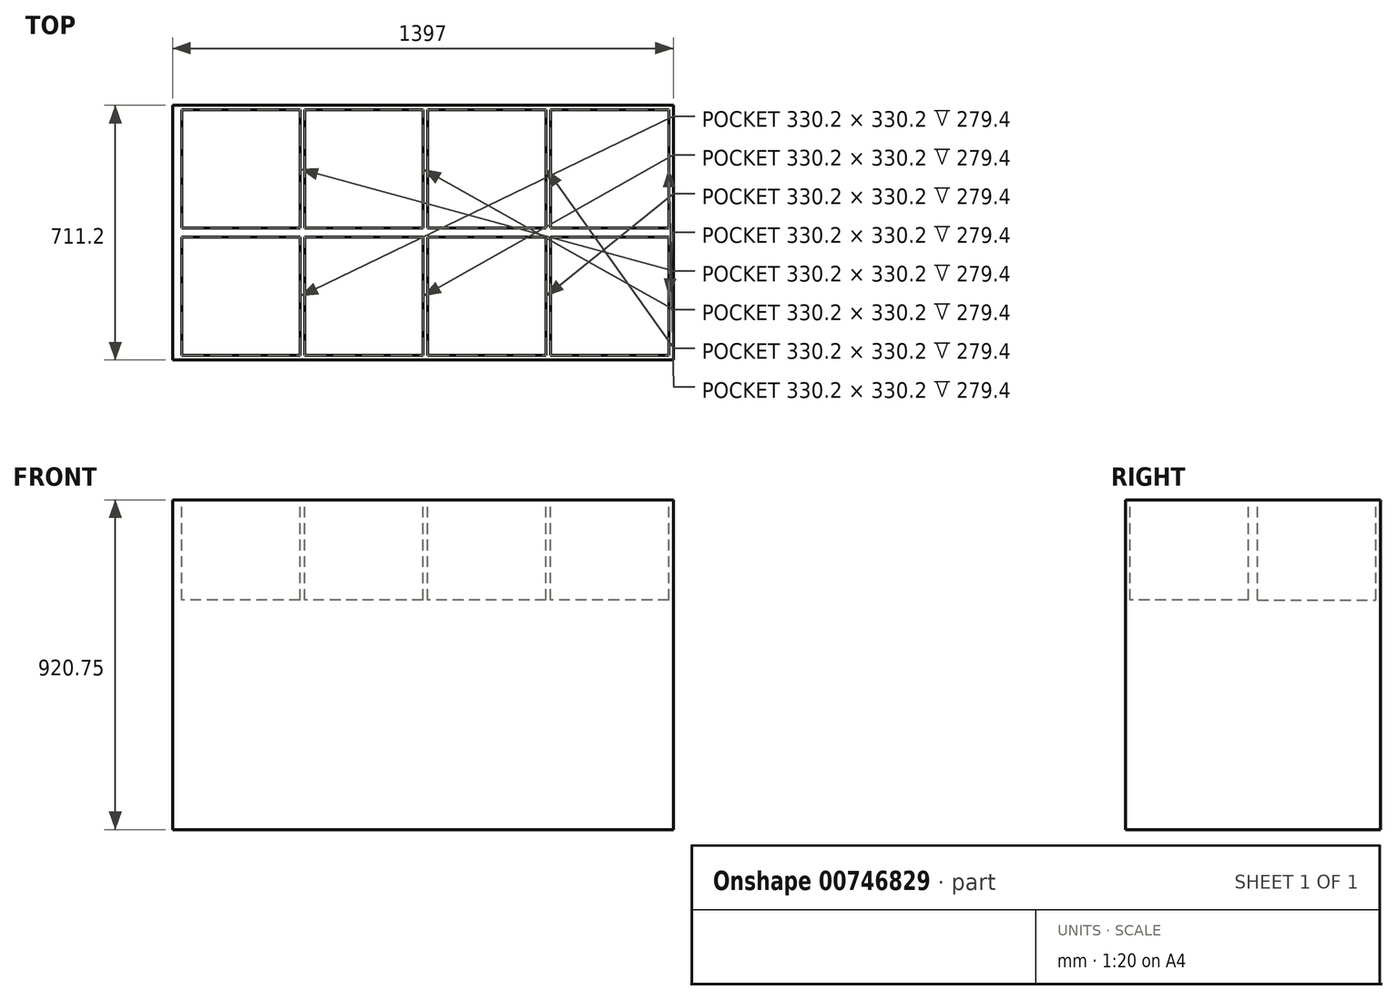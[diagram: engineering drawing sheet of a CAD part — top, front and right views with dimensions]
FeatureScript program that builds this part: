
annotation { "Feature Type Name" : "Feature", "Feature Type Description" : "" }
export const myFeature = defineFeature(function(context is Context, id is Id, definition is map)
    precondition{}
    {
        {
            var Q0;
            Q0=qCreatedBy(makeId("Top.planeOp"),FACE);
            var sketch = newSketch(context, id + "F0", { "sketchPlane" : qUnion([Q0])});
            skLineSegment(sketch, "E0.bottom", {"start": v(0, 0) * mm, "end": v(1397, 0) * mm});
            skLineSegment(sketch, "E0.top", {"start": v(0, -355.6) * mm, "end": v(1397, -355.6) * mm});
            skLineSegment(sketch, "E0.left", {"start": v(0, 0) * mm, "end": v(0, -355.6) * mm});
            skLineSegment(sketch, "E0.right", {"start": v(1397, 0) * mm, "end": v(1397, -355.6) * mm});
            skSolve(sketch);
        }
        {
            var Q0;
            Q0 = qSketchRegion(id + "F0", true);
            extrude(context, id + "F1", {"entities" : qUnion([Q0]), "depth" : 920.75 * mm, "offsetDistance" : 25.4 * mm});
        }
        {
            var Q0;
            Q0=makeQuery(id+"F1.opExtrude","CAP_FACE",FACE,{"disambiguationData":[OSD([sQuery(id+"F0.wireOp",EDGE,"E0.bottom"),sQuery(id+"F0.wireOp",EDGE,"E0.top"),sQuery(id+"F0.wireOp",EDGE,"E0.left"),sQuery(id+"F0.wireOp",EDGE,"E0.right")])],"isStart":false});
            var sketch = newSketch(context, id + "F2", { "sketchPlane" : qUnion([Q0])});
            skLineSegment(sketch, "E1.bottom", {"start": v(1397, -355.6) * mm, "end": v(1384.3, -355.6) * mm});
            skLineSegment(sketch, "E1.top", {"start": v(1397, -342.9) * mm, "end": v(1384.3, -342.9) * mm});
            skLineSegment(sketch, "E1.left", {"start": v(1397, -355.6) * mm, "end": v(1397, -342.9) * mm});
            skLineSegment(sketch, "E1.right", {"start": v(1384.3, -355.6) * mm, "end": v(1384.3, -342.9) * mm});
            skSolve(sketch);
        }
        {
            var Q0;
            {var subQ4=sQuery(id+"F2.wireOp",EDGE,"E1.top");Q0=makeQuery(id+"F2.imprint","IMPRINT",FACE,{"disambiguationData":[TD([[makeQuery(id+"F2.imprint","IMPRINT",EDGE,{"derivedFrom":subQ4}),-1.0]])]});}
            var sketch = newSketch(context, id + "F3", { "sketchPlane" : qUnion([Q0])});
            skLineSegment(sketch, "E2.bottom", {"start": v(1384.3, -342.9) * mm, "end": v(1054.1, -342.9) * mm});
            skLineSegment(sketch, "E2.top", {"start": v(1384.3, -12.7) * mm, "end": v(1054.1, -12.7) * mm});
            skLineSegment(sketch, "E2.left", {"start": v(1384.3, -342.9) * mm, "end": v(1384.3, -12.7) * mm});
            skLineSegment(sketch, "E2.right", {"start": v(1054.1, -342.9) * mm, "end": v(1054.1, -12.7) * mm});
            skSolve(sketch);
        }
        {
            var Q0;
            {var subQ4=sQuery(id+"F2.wireOp",EDGE,"E1.top");Q0=makeQuery(id+"F2.imprint","IMPRINT",FACE,{"disambiguationData":[TD([[makeQuery(id+"F2.imprint","IMPRINT",EDGE,{"derivedFrom":subQ4}),-1.0]])]});}
            var sketch = newSketch(context, id + "F4", { "sketchPlane" : qUnion([Q0])});
            skLineSegment(sketch, "E3", {"start": v(1054.1, -12.7) * mm, "end": v(1041.4, -12.7) * mm});
            skSolve(sketch);
        }
        {
            var Q0;
            {var subQ4=sQuery(id+"F2.wireOp",EDGE,"E1.top");Q0=makeQuery(id+"F4.imprint","IMPRINT",FACE,{"disambiguationData":[TD([[makeQuery(id+"F4.imprint","IMPRINT",EDGE,{"derivedFrom":makeQuery(id+"F2.imprint","IMPRINT",EDGE,{"derivedFrom":subQ4})}),-1.0]])]});}
            var sketch = newSketch(context, id + "F5", { "sketchPlane" : qUnion([Q0])});
            skLineSegment(sketch, "E4.bottom", {"start": v(1041.4, -12.7) * mm, "end": v(711.2, -12.7) * mm});
            skLineSegment(sketch, "E4.top", {"start": v(1041.4, -342.9) * mm, "end": v(711.2, -342.9) * mm});
            skLineSegment(sketch, "E4.left", {"start": v(1041.4, -12.7) * mm, "end": v(1041.4, -342.9) * mm});
            skLineSegment(sketch, "E4.right", {"start": v(711.2, -12.7) * mm, "end": v(711.2, -342.9) * mm});
            skSolve(sketch);
        }
        {
            var Q0;
            {var subQ4=sQuery(id+"F2.wireOp",EDGE,"E1.top");Q0=makeQuery(id+"F4.imprint","IMPRINT",FACE,{"disambiguationData":[TD([[makeQuery(id+"F4.imprint","IMPRINT",EDGE,{"derivedFrom":makeQuery(id+"F2.imprint","IMPRINT",EDGE,{"derivedFrom":subQ4})}),-1.0]])]});}
            var sketch = newSketch(context, id + "F6", { "sketchPlane" : qUnion([Q0])});
            skLineSegment(sketch, "E5", {"start": v(711.2, -12.7) * mm, "end": v(698.5, -12.7) * mm});
            skSolve(sketch);
        }
        {
            var Q0;
            {var subQ4=sQuery(id+"F2.wireOp",EDGE,"E1.top");Q0=makeQuery(id+"F4.imprint","IMPRINT",FACE,{"disambiguationData":[TD([[makeQuery(id+"F4.imprint","IMPRINT",EDGE,{"derivedFrom":makeQuery(id+"F2.imprint","IMPRINT",EDGE,{"derivedFrom":subQ4})}),-1.0]])]});}
            var sketch = newSketch(context, id + "F7", { "sketchPlane" : qUnion([Q0])});
            skLineSegment(sketch, "E6.bottom", {"start": v(698.5, -12.7) * mm, "end": v(368.3, -12.7) * mm});
            skLineSegment(sketch, "E6.top", {"start": v(698.5, -342.9) * mm, "end": v(368.3, -342.9) * mm});
            skLineSegment(sketch, "E6.left", {"start": v(698.5, -12.7) * mm, "end": v(698.5, -342.9) * mm});
            skLineSegment(sketch, "E6.right", {"start": v(368.3, -12.7) * mm, "end": v(368.3, -342.9) * mm});
            skSolve(sketch);
        }
        {
            var Q0;
            {var subQ4=sQuery(id+"F2.wireOp",EDGE,"E1.top");Q0=makeQuery(id+"F4.imprint","IMPRINT",FACE,{"disambiguationData":[TD([[makeQuery(id+"F4.imprint","IMPRINT",EDGE,{"derivedFrom":makeQuery(id+"F2.imprint","IMPRINT",EDGE,{"derivedFrom":subQ4})}),-1.0]])]});}
            var sketch = newSketch(context, id + "F8", { "sketchPlane" : qUnion([Q0])});
            skLineSegment(sketch, "E7", {"start": v(368.3, -12.7) * mm, "end": v(355.6, -12.7) * mm});
            skSolve(sketch);
        }
        {
            var Q0;
            {var subQ4=sQuery(id+"F2.wireOp",EDGE,"E1.top");Q0=makeQuery(id+"F4.imprint","IMPRINT",FACE,{"disambiguationData":[TD([[makeQuery(id+"F4.imprint","IMPRINT",EDGE,{"derivedFrom":makeQuery(id+"F2.imprint","IMPRINT",EDGE,{"derivedFrom":subQ4})}),-1.0]])]});}
            var sketch = newSketch(context, id + "F9", { "sketchPlane" : qUnion([Q0])});
            skLineSegment(sketch, "E8.bottom", {"start": v(355.6, -12.7) * mm, "end": v(25.4, -12.7) * mm});
            skLineSegment(sketch, "E8.top", {"start": v(355.6, -342.9) * mm, "end": v(25.4, -342.9) * mm});
            skLineSegment(sketch, "E8.left", {"start": v(355.6, -12.7) * mm, "end": v(355.6, -342.9) * mm});
            skLineSegment(sketch, "E8.right", {"start": v(25.4, -12.7) * mm, "end": v(25.4, -342.9) * mm});
            skSolve(sketch);
        }
        {
            var Q0;
            Q0 = qSketchRegion(id + "F9", true);
            extrude(context, id + "F10", {"entities" : qUnion([Q0]), "operationType" : NewBodyOperationType.REMOVE, "oppositeDirection" : true, "depth" : 279.4 * mm, "offsetDistance" : 25.4 * mm});
        }
        {
            var Q0;
            Q0 = qSketchRegion(id + "F7", true);
            extrude(context, id + "F11", {"entities" : qUnion([Q0]), "operationType" : NewBodyOperationType.REMOVE, "oppositeDirection" : true, "depth" : 279.4 * mm, "offsetDistance" : 25.4 * mm});
        }
        {
            var Q0;
            Q0 = qSketchRegion(id + "F5", true);
            extrude(context, id + "F12", {"entities" : qUnion([Q0]), "operationType" : NewBodyOperationType.REMOVE, "oppositeDirection" : true, "depth" : 279.4 * mm, "offsetDistance" : 25.4 * mm});
        }
        {
            var Q0;
            Q0 = qSketchRegion(id + "F3", true);
            extrude(context, id + "F13", {"entities" : qUnion([Q0]), "operationType" : NewBodyOperationType.REMOVE, "oppositeDirection" : true, "depth" : 279.4 * mm, "offsetDistance" : 25.4 * mm});
        }
        {
            var Q0;
            Q0=makeQuery(id+"F1.opExtrude","SWEPT_BODY",BODY,{"disambiguationData":[OSD([sQuery(id+"F0.wireOp",EDGE,"E0.bottom"),sQuery(id+"F0.wireOp",EDGE,"E0.top"),sQuery(id+"F0.wireOp",EDGE,"E0.left"),sQuery(id+"F0.wireOp",EDGE,"E0.right")])]});
            var Q1;
            Q1=qCreatedBy(makeId("Front.planeOp"),FACE);
            mirror(context, id + "F14", {"operationType" : NewBodyOperationType.ADD, "entities" : qUnion([Q0]), "mirrorPlane" : qUnion([Q1])});
        }
    });
